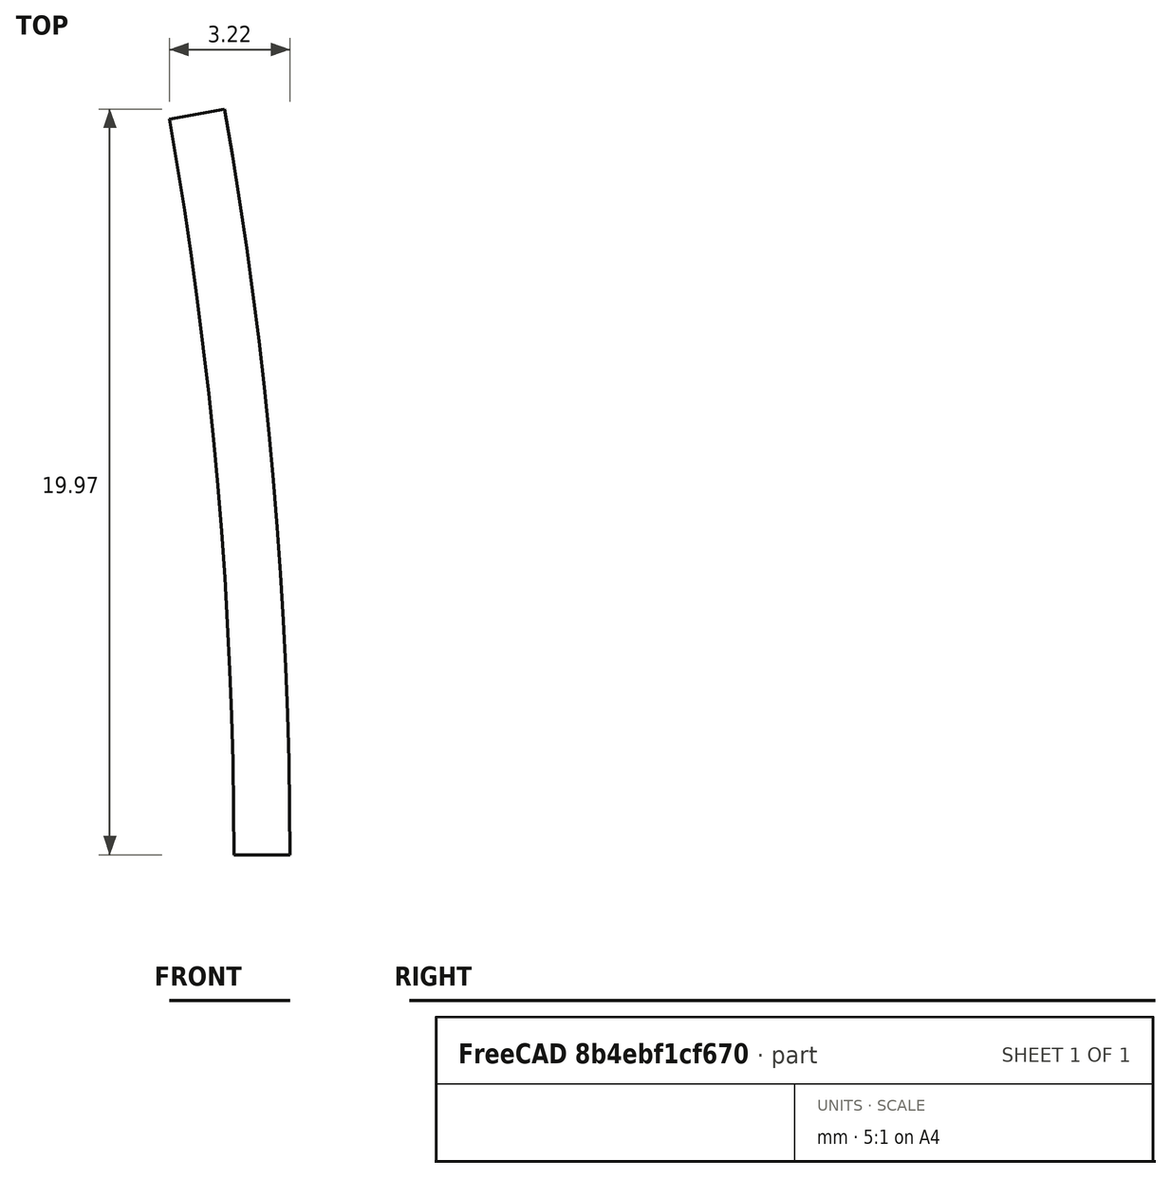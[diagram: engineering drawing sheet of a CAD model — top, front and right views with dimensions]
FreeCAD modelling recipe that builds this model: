
FCSTD DOCUMENT  (FreeCAD 0.18R4 (GitTag))
Label: ring1
License: All rights reserved
LicenseURL: http://en.wikipedia.org/wiki/All_rights_reserved
objects: Sketcher::SketchObject×3, PartDesign::Body×2, Spreadsheet::Sheet×1, Surface::Filling×1
note: 6 computed .brp shape members not serialized (recipe doc carries the construction recipe); baked Part::Feature solids carry a one-line shape summary decoded from their .brp

FEATURE [Spreadsheet::Sheet] Spreadsheet  label="Variables"
  cells = A2=segmentNumber; B2(segmentNumber)=36; A3=outerDiameter; B3(outerDiameter)=230; D3=Calc Value; A4=innerDiameter; B4(innerDiameter)=227; D4=Input Value; A5=length; B5(length)=20; A6=segmentAngle; B6(segmentAngle)==360 / segmentNumber; A7=axialMisalignment; B7(axialMisalignment)=0.5
FEATURE [Sketcher::SketchObject] Sketch003  label="RingSketch"
  MapMode = 5
  Support = -> [XY_Plane]
  expr: Constraints[15] = Variables.outerDiameter / 2
  expr: Constraints[14] = Variables.innerDiameter / 2
  expr: Constraints[0] = Variables.segmentAngle
  sketch-geometry (6):
    g0: LineSegment StartX=113.5 StartY=2.46647e-10 StartZ=0 EndX=115 EndY=2.49573e-10 EndZ=0
    g1: LineSegment StartX=111.776 StartY=19.7091 StartZ=0 EndX=113.253 EndY=19.9695 EndZ=0
    g2: LineSegment [constr] StartX=0 StartY=0 StartZ=0 EndX=113.5 EndY=2.46647e-10 EndZ=0
    g3: LineSegment [constr] StartX=0 StartY=0 StartZ=0 EndX=111.776 EndY=19.7091 EndZ=0
    g4: ArcOfCircle CenterX=0 CenterY=0 CenterZ=0 NormalX=0 NormalY=0 NormalZ=1 AngleXU=0 Radius=115 StartAngle=2.1702e-12 EndAngle=0.174533
    g5: ArcOfCircle CenterX=0 CenterY=0 CenterZ=0 NormalX=0 NormalY=0 NormalZ=1 AngleXU=0 Radius=113.5 StartAngle=2.1731e-12 EndAngle=0.174533
  constraints (16):
    c: Angle(g0,g1) = 0.174533
    c: Coincident(g2,g-1)
    c: Coincident(g2,g0)
    c: Coincident(g3,g2)
    c: Coincident(g3,g1)
    c: Parallel(g2,g0)
    c: Parallel(g3,g1)
    c: Coincident(g4,g-1)
    c: Coincident(g4,g0)
    c: Coincident(g4,g1)
    c: Coincident(g5,g4)
    c: Coincident(g5,g1)
    c: Coincident(g5,g0)
    c: Angle(g-1,g2) = 0
    c: Radius(g5) = 113.5
    c: Radius(g4) = 115
FEATURE [Sketcher::SketchObject] Sketch  label="BoundingBox"
  MapMode = 5
  Support = -> [XY_Plane]
  expr: Constraints[13] = Variables.outerDiameter
  expr: Constraints[8] = Variables.outerDiameter
  sketch-geometry (6):
    g0: LineSegment StartX=-115 StartY=-115 StartZ=0 EndX=115 EndY=-115 EndZ=0
    g1: LineSegment StartX=115 StartY=-115 StartZ=0 EndX=115 EndY=115 EndZ=0
    g2: LineSegment StartX=115 StartY=115 StartZ=0 EndX=-115 EndY=115 EndZ=0
    g3: LineSegment StartX=-115 StartY=115 StartZ=0 EndX=-115 EndY=-115 EndZ=0
    g4: LineSegment [constr] StartX=-115 StartY=-115 StartZ=0 EndX=115 EndY=115 EndZ=0
    g5: GeomPoint X=0 Y=0 Z=0
  constraints (14):
    c: Coincident(g0,g1)
    c: Coincident(g1,g2)
    c: Coincident(g2,g3)
    c: Coincident(g3,g0)
    c: Horizontal(g0)
    c: Horizontal(g2)
    c: Vertical(g1)
    c: Vertical(g3)
    c: DistanceY(g1,g1) = 230
    c: Coincident(g4,g0)
    c: Coincident(g4,g1)
    c: Symmetric(g0,g1,g5)
    c: Coincident(g-1,g5)
    c: DistanceX(g2,g2) = 230
FEATURE [PartDesign::Body] Body  label="TopView"
  Group = -> [Sketch003,Sketch]
  Origin = -> Origin
FEATURE [Sketcher::SketchObject] Sketch004  label="RingSide"
  MapMode = 5
  Support = -> [XY_Plane001]
  expr: Constraints[15] = Variables.outerDiameter
  expr: Constraints[12] = Variables.length
  expr: Constraints[22] = Variables.length / 2 - Variables.axialMisalignment
  expr: Constraints[14] = Variables.innerDiameter
  sketch-geometry (8):
    g0: LineSegment StartX=-9.5 StartY=113.5 StartZ=0 EndX=10.5 EndY=113.5 EndZ=0
    g1: LineSegment StartX=10.5 StartY=113.5 StartZ=0 EndX=10.5 EndY=115 EndZ=0
    g2: LineSegment StartX=10.5 StartY=115 StartZ=0 EndX=-9.5 EndY=115 EndZ=0
    g3: LineSegment StartX=-9.5 StartY=115 StartZ=0 EndX=-9.5 EndY=113.5 EndZ=0
    g4: LineSegment StartX=-9.5 StartY=-113.5 StartZ=0 EndX=10.5 EndY=-113.5 EndZ=0
    g5: LineSegment StartX=10.5 StartY=-113.5 StartZ=0 EndX=10.5 EndY=-115 EndZ=0
    g6: LineSegment StartX=10.5 StartY=-115 StartZ=0 EndX=-9.5 EndY=-115 EndZ=0
    g7: LineSegment StartX=-9.5 StartY=-115 StartZ=0 EndX=-9.5 EndY=-113.5 EndZ=0
  constraints (23):
    c: Coincident(g0,g1)
    c: Coincident(g1,g2)
    c: Coincident(g2,g3)
    c: Coincident(g3,g0)
    c: Horizontal(g2)
    c: Vertical(g1)
    c: Coincident(g4,g5)
    c: Coincident(g5,g6)
    c: Coincident(g6,g7)
    c: Coincident(g7,g4)
    c: Horizontal(g6)
    c: Vertical(g5)
    c: DistanceX(g6,g6) = 20
    c: Equal(g6,g0)
    c: DistanceY(g4,g0) = 227
    c: DistanceY(g5,g1) = 230
    c: Equal(g1,g5)
    c: Symmetric(g4,g0,g-1)
    c: Vertical(g3)
    c: Angle(g0,g3) = 1.5708
    c: Angle(g7,g4) = 1.5708
    c: Angle(g4,g5) = 1.5708
    c: DistanceX(g2,g-1) = 9.5
FEATURE [PartDesign::Body] Body001  label="SideView"
  Group = -> [Sketch004]
  Origin = -> Origin001
FEATURE [Surface::Filling] Surface  label="RingSketch_Surface"
  Anisotropy = false
  BoundaryEdges = -> [Sketch003]
  BoundaryOrder = [0,0,0,0]
  Degree = 3
  Iterations = 2
  MaximumDegree = 8
  MaximumSegments = 9
  PointsOnCurve = 15
  TolAngular = 0.01
  TolCurvature = 0.1
  Tolerance2d = 1e-05
  Tolerance3d = 0.0001
